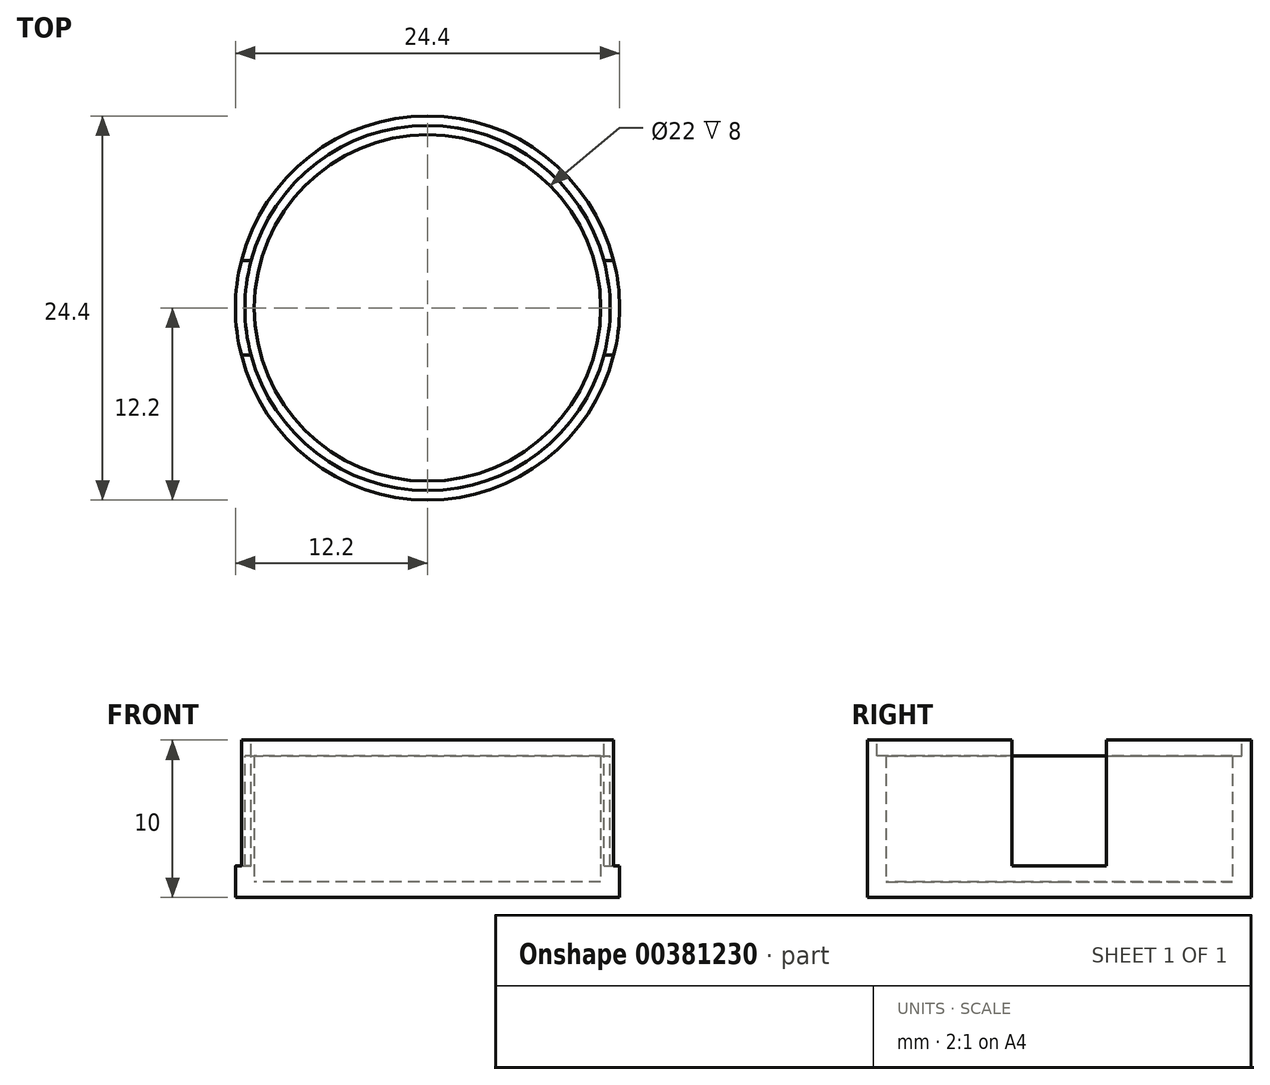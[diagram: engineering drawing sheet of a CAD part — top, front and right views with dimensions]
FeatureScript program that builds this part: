
annotation { "Feature Type Name" : "Feature", "Feature Type Description" : "" }
export const myFeature = defineFeature(function(context is Context, id is Id, definition is map)
    precondition{}
    {
        {
            var Q0;
            Q0=qCreatedBy(makeId("Top.planeOp"),FACE);
            var sketch = newSketch(context, id + "F0", { "sketchPlane" : qUnion([Q0])});
            skCircle(sketch, "E0", {"center": v(-31.58, 0) * mm, "radius": 11 * mm});
            skCircle(sketch, "E1", {"center": v(-31.58, 0) * mm, "radius": 12.2 * mm});
            skSolve(sketch);
        }
        {
            var Q0;
            Q0=makeQuery(id+"F0.imprint","IMPRINT",FACE,{"disambiguationData":[TD([[makeQuery(id+"F0.imprint","IMPRINT",EDGE,{"derivedFrom":sQuery(id+"F0.wireOp",EDGE,"E0")}),1.0]])]});
            extrude(context, id + "F1", {"entities" : qUnion([Q0]), "depth" : 1 * mm, "offsetDistance" : 25 * mm});
        }
        {
            var Q0;
            Q0=makeQuery(id+"F0.imprint","IMPRINT",FACE,{"disambiguationData":[TD([[makeQuery(id+"F0.imprint","IMPRINT",EDGE,{"derivedFrom":sQuery(id+"F0.wireOp",EDGE,"E0")}),-1.0]])]});
            extrude(context, id + "F2", {"entities" : qUnion([Q0]), "operationType" : NewBodyOperationType.ADD, "depth" : 10 * mm, "offsetDistance" : 25 * mm});
        }
        {
            var Q0;
            Q0=makeQuery(id+"F2.opExtrude","CAP_FACE",FACE,{"disambiguationData":[OSD([sQuery(id+"F0.wireOp",EDGE,"E0"),sQuery(id+"F0.wireOp",EDGE,"E1")])],"isStart":false});
            var sketch = newSketch(context, id + "F3", { "sketchPlane" : qUnion([Q0])});
            skCircle(sketch, "E2", {"center": v(-31.58, 0) * mm, "radius": 11.6 * mm});
            skSolve(sketch);
        }
        {
            var Q0;
            Q0=makeQuery(id+"F3.imprint","IMPRINT",FACE,{"disambiguationData":[TD([[makeQuery(id+"F3.imprint","IMPRINT",EDGE,{"derivedFrom":sQuery(id+"F3.wireOp",EDGE,"E2")}),1.0]])]});
            extrude(context, id + "F4", {"entities" : qUnion([Q0]), "operationType" : NewBodyOperationType.REMOVE, "oppositeDirection" : true, "depth" : 1 * mm, "offsetDistance" : 25 * mm});
        }
        {
            var Q0;
            Q0=makeQuery(id+"F2.opExtrude","CAP_FACE",FACE,{"disambiguationData":[OSD([sQuery(id+"F0.wireOp",EDGE,"E0"),sQuery(id+"F0.wireOp",EDGE,"E1")])],"isStart":false});
            var sketch = newSketch(context, id + "F5", { "sketchPlane" : qUnion([Q0])});
            skLineSegment(sketch, "E3.bottom", {"start": v(-48.4, 3) * mm, "end": v(-13.74, 3) * mm});
            skLineSegment(sketch, "E3.top", {"start": v(-48.4, -3) * mm, "end": v(-13.74, -3) * mm});
            skLineSegment(sketch, "E3.left", {"start": v(-48.4, 3) * mm, "end": v(-48.4, -3) * mm});
            skLineSegment(sketch, "E3.right", {"start": v(-13.74, 3) * mm, "end": v(-13.74, -3) * mm});
            skLineSegment(sketch, "E4", {"start": v(-31.06, 3) * mm, "end": v(-31.06, 12.19) * mm, "construction": true});
            skLineSegment(sketch, "E5", {"start": v(-31.06, -3) * mm, "end": v(-31.06, -12.19) * mm, "construction": true});
            skSolve(sketch);
        }
        {
            var Q0;
            {var subQ0=sQuery(id+"F5.wireOp",EDGE,"E3.bottom");var subQ1=makeQuery(id+"F2.opExtrude","CAP_EDGE",EDGE,{"disambiguationData":[OSD([sQuery(id+"F0.wireOp",EDGE,"E1")])],"isStart":false});var subQ2=makeQuery(id+"F5.imprint","INTERSECT",VERTEX,{"disambiguationData":[OD(1.0)],"derivedFrom":[subQ1,subQ0]});Q0=makeQuery(id+"F5.imprint","IMPRINT",FACE,{"disambiguationData":[TD([[makeQuery(id+"F5.imprint","IMPRINT",EDGE,{"disambiguationData":[TD([[subQ2,1.0]])],"derivedFrom":subQ0}),-1.0]])]});}
            var Q1;
            {var subQ0=sQuery(id+"F5.wireOp",EDGE,"E3.bottom");var subQ1=makeQuery(id+"F4.boolean.opBoolean","COPY",EDGE,{"derivedFrom":makeQuery(id+"F4.opExtrude","CAP_EDGE",EDGE,{"disambiguationData":[OSD([sQuery(id+"F3.wireOp",EDGE,"E2")])],"isStart":true})});var subQ2=makeQuery(id+"F5.imprint","INTERSECT",VERTEX,{"disambiguationData":[OD(0.0)],"derivedFrom":[subQ1,subQ0]});Q1=makeQuery(id+"F5.imprint","IMPRINT",FACE,{"disambiguationData":[TD([[makeQuery(id+"F5.imprint","IMPRINT",EDGE,{"disambiguationData":[TD([[subQ2,-1.0]])],"derivedFrom":subQ0}),-1.0]])]});}
            var Q2;
            {var subQ0=sQuery(id+"F5.wireOp",EDGE,"E3.bottom");var subQ1=makeQuery(id+"F2.opExtrude","CAP_EDGE",EDGE,{"disambiguationData":[OSD([sQuery(id+"F0.wireOp",EDGE,"E1")])],"isStart":false});var subQ2=makeQuery(id+"F5.imprint","INTERSECT",VERTEX,{"disambiguationData":[OD(0.0)],"derivedFrom":[subQ1,subQ0]});Q2=makeQuery(id+"F5.imprint","IMPRINT",FACE,{"disambiguationData":[TD([[makeQuery(id+"F5.imprint","IMPRINT",EDGE,{"disambiguationData":[TD([[subQ2,-1.0]])],"derivedFrom":subQ0}),-1.0]])]});}
            extrude(context, id + "F6", {"entities" : qUnion([Q0, Q1, Q2]), "operationType" : NewBodyOperationType.REMOVE, "oppositeDirection" : true, "depth" : 8 * mm, "offsetDistance" : 25 * mm});
        }
    });
